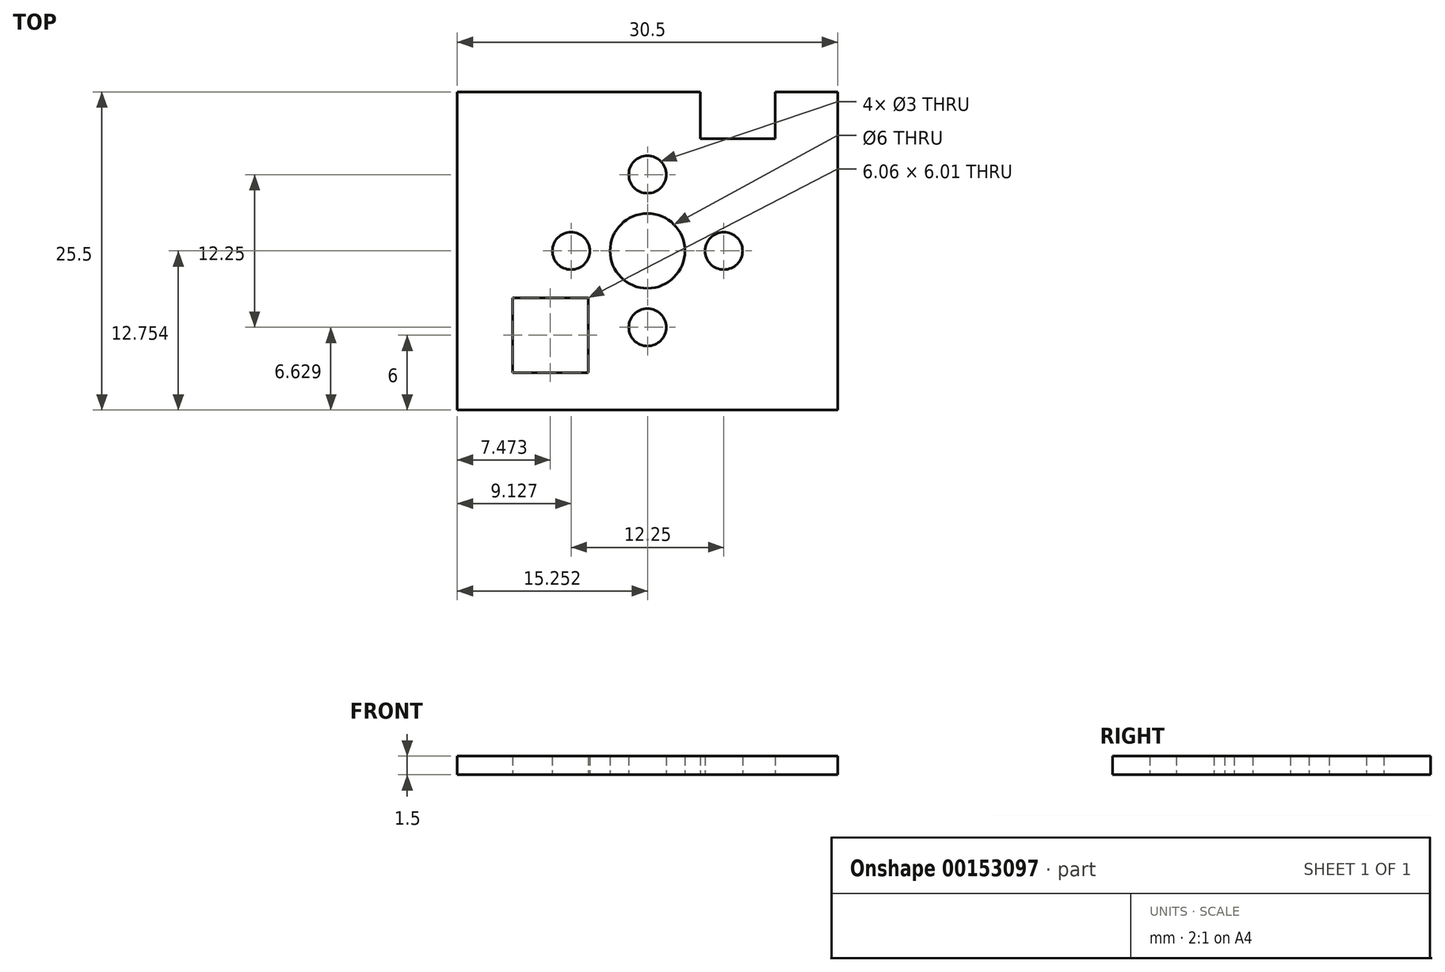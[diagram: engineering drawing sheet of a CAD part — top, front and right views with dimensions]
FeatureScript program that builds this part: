
annotation { "Feature Type Name" : "Feature", "Feature Type Description" : "" }
export const myFeature = defineFeature(function(context is Context, id is Id, definition is map)
    precondition{}
    {
        {
            var Q0;
            Q0=qCreatedBy(makeId("Top.planeOp"),FACE);
            var sketch = newSketch(context, id + "F0", { "sketchPlane" : qUnion([Q0])});
            skLineSegment(sketch, "E0.top", {"start": v(-39.99, 1.92) * mm, "end": v(-9.49, 1.92) * mm});
            skLineSegment(sketch, "E0.left", {"start": v(-39.99, 27.42) * mm, "end": v(-39.99, 1.92) * mm});
            skLineSegment(sketch, "E0.right", {"start": v(-9.49, 27.42) * mm, "end": v(-9.49, 1.92) * mm});
            skLineSegment(sketch, "E1", {"start": v(-24.74, 27.42) * mm, "end": v(-24.74, 1.92) * mm, "construction": true});
            skLineSegment(sketch, "E2", {"start": v(-39.99, 14.67) * mm, "end": v(-9.49, 14.67) * mm, "construction": true});
            skCircle(sketch, "E3", {"center": v(-24.74, 14.67) * mm, "radius": 3 * mm});
            skLineSegment(sketch, "E4.bottom", {"start": v(-39.99, 1.92) * mm, "end": v(-29.49, 1.92) * mm, "construction": true});
            skLineSegment(sketch, "E4.left", {"start": v(-39.99, 1.92) * mm, "end": v(-39.99, 10.92) * mm, "construction": true});
            skLineSegment(sketch, "E4.right", {"start": v(-29.49, 1.92) * mm, "end": v(-29.49, 6.42) * mm, "construction": true});
            skLineSegment(sketch, "E5.left", {"start": v(-9.49, 27.42) * mm, "end": v(-9.49, 23.67) * mm, "construction": true});
            skLineSegment(sketch, "E5.right", {"start": v(-20.49, 27.42) * mm, "end": v(-20.49, 23.67) * mm, "construction": true});
            skLineSegment(sketch, "E6", {"start": v(-39.99, 27.42) * mm, "end": v(-20.49, 27.42) * mm});
            skLineSegment(sketch, "E7", {"start": v(-20.49, 23.67) * mm, "end": v(-14.49, 23.67) * mm});
            skCircle(sketch, "E8", {"center": v(-24.74, 14.67) * mm, "radius": 7.83 * mm, "construction": true});
            skCircle(sketch, "E9", {"center": v(-32.56, 14.67) * mm, "radius": 1.5 * mm, "construction": true});
            skCircle(sketch, "E10", {"center": v(-16.91, 14.67) * mm, "radius": 1.5 * mm, "construction": true});
            skCircle(sketch, "E11", {"center": v(-24.74, 14.67) * mm, "radius": 6.12 * mm, "construction": true});
            skCircle(sketch, "E12", {"center": v(-24.74, 20.8) * mm, "radius": 1.5 * mm});
            skCircle(sketch, "E13", {"center": v(-24.74, 8.55) * mm, "radius": 1.5 * mm});
            skLineSegment(sketch, "E14", {"start": v(-20.49, 27.42) * mm, "end": v(-20.49, 23.67) * mm});
            skLineSegment(sketch, "E15", {"start": v(-14.49, 23.67) * mm, "end": v(-14.49, 27.42) * mm});
            skLineSegment(sketch, "E16", {"start": v(-9.49, 27.42) * mm, "end": v(-14.49, 27.42) * mm});
            skLineSegment(sketch, "E17", {"start": v(-29.49, 4.92) * mm, "end": v(-36.99, 4.92) * mm});
            skCircle(sketch, "E18", {"center": v(-18.61, 14.67) * mm, "radius": 1.5 * mm});
            skCircle(sketch, "E19", {"center": v(-30.86, 14.67) * mm, "radius": 1.5 * mm});
            skLineSegment(sketch, "E20", {"start": v(-36.99, 4.92) * mm, "end": v(-39.99, 4.92) * mm, "construction": true});
            skLineSegment(sketch, "E21", {"start": v(-36.99, 4.92) * mm, "end": v(-18.85, 4.92) * mm, "construction": true});
            skLineSegment(sketch, "E22", {"start": v(-29.49, 4.92) * mm, "end": v(-29.49, 10.92) * mm});
            skLineSegment(sketch, "E23.bottom", {"start": v(-29.49, 4.92) * mm, "end": v(-35.55, 4.92) * mm});
            skLineSegment(sketch, "E23.top", {"start": v(-29.49, 10.92) * mm, "end": v(-35.55, 10.92) * mm});
            skLineSegment(sketch, "E23.right", {"start": v(-35.55, 4.92) * mm, "end": v(-35.55, 10.92) * mm});
            skSolve(sketch);
        }
        {
            var Q0;
            Q0=makeQuery(id+"F0.imprint","IMPRINT",FACE,{"disambiguationData":[TD([[makeQuery(id+"F0.imprint","IMPRINT",EDGE,{"derivedFrom":sQuery(id+"F0.wireOp",EDGE,"E0.top")}),1.0]])]});
            extrude(context, id + "F1", {"entities" : qUnion([Q0]), "depth" : 1.5 * mm});
        }
    });
